# Revit family: Track_light_single
name_source: partatom
category: Lighting Fixtures
revit_build: Autodesk Revit 2016 (Build: 20150220_1215(x64)
units: mm (PartAtom-declared; Revit-internal decimal feet)

## family parameters
Always vertical = Yes
Cut with Voids When Loaded = No
Host = Ceiling
Light Source = Yes
Part Type = Normal
Room Calculation Point = No
Round Connector Dimension = Use Diameter
Shared = No
Work Plane-Based = No

## types (6) — shared parameters
Dimming Lamp Color Temperature Shift = <None>
Light Source Symbol Length = 120"
OffstDown = 0"
distance between lights = 25"

## per-type parameters (varying)
| type | Color Filter | Spot Beam Angle | Spot Field Angle | Tilt Angle |
| Track_light_adjustable_3686 2 | 16777215 | 30.00° | 45.00° | 60.00° |
| Track_light_adjustable_10 | 16777215 | 90.00° | 80.00° | 40.00° |
| Track_light_adjustable_5 | 16777215 | 60.00° | 45.00° | 20.00° |
| Track_light_adjustable_4 | 16777215 | 120.00° | 120.00° | 5.00° |
| Track_light_adjustable_2 | 8453888 | 90.00° | 90.00° | 60.00° |
| Track_light_adjustable_1 | 16777088 | 120.00° | 120.00° | 5.00° |

## geometry (parser evidence)
native form markers: Blend x2, Sweep x9
no freeform markers — native parametric forms only
